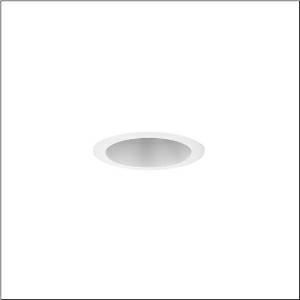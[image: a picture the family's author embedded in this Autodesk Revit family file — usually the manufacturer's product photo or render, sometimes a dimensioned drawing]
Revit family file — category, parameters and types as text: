
# Revit family: lunis_31_mini_51dn157e31
name_source: partatom
category: Lighting Fixtures
units: mm (PartAtom-declared; Revit-internal decimal feet)

## family parameters
Cut with Voids When Loaded = No
Host = Face
Light Source = No
Part Type = Normal
Room Calculation Point = No
Round Connector Dimension = Use Diameter
Shared = No

## types (1)
- Lunis 31 mini (1 x LED, 1000 lm, 8.3 W, 3000K)
    Apparent Load = 8 VA
    CIE Flux Codes = 93 98 100 100 100
    Color Rendering = 80
    Color Temperature = 3000K
    Default Elevation = 1800 mm
    Description = Lunis 31,  mini, downlight, light control with lens, light emission: direct distribution, LED rated luminous flux: 1.000lm, light colour: 830, mains connection: 220..240V, AC, 50/60Hz, housing, white, protection rating (complete): IP20, protection rating (on room side): IP54, insulation class (complete): insulation class II (safety insulation), certification: CE, packaging unit: 1 piece
    Height = 0 mm  [stored 0 ft]
    Lamp = 1 x LED
    Lamp Light Flux = 1000 lm
    Lamp Power = 8.3 W
    Lamp count = 1
    Length = 188 mm  [stored 0.616798 ft]
    Luminous efficacy = 120 lm/W
    Manufacturer = Siteco
    ModVariant = No
    Model = 51DN157E31
    Mounting Place = Ceiling
    Mounting Type = Recessed
    Number of Poles = 1
    OnlyDefault = Yes
    Power Factor = 1
    Product Name = Lunis 31 mini
    Product group = downlight
    ProductGroupID = 400
    Protection Class = Protection class II
    Protection Degree = IP 20
    RLX_Detail_Level = 1
    RLX_Emergency_Light_Flux = 0 lm
    RLX_Emergency_Type = 0
    RLX_Emergency_Type_DB = No
    RlxData = <blob elided: 21737 chars, md5=269d8b93>
    Socket = socket
    Standby Power = 0 W
    System Light Flux = 1000 lm
    System Power = 8 W
    Type Comments = Product without accessories
    Type Image = l_1345911.jpg
    URL = http://relux.com
    VarID = ---
    Voltage = 0 V
    Weight = 0.00 kg
    Width = 0 mm  [stored 0 ft]

note: [stored X ft] marks values corroborated as IEEE doubles in the binary element streams (Revit-internal decimal feet)

## geometry (parser evidence)
native form markers: Blend x4, Sweep x11
no freeform markers — native parametric forms only
